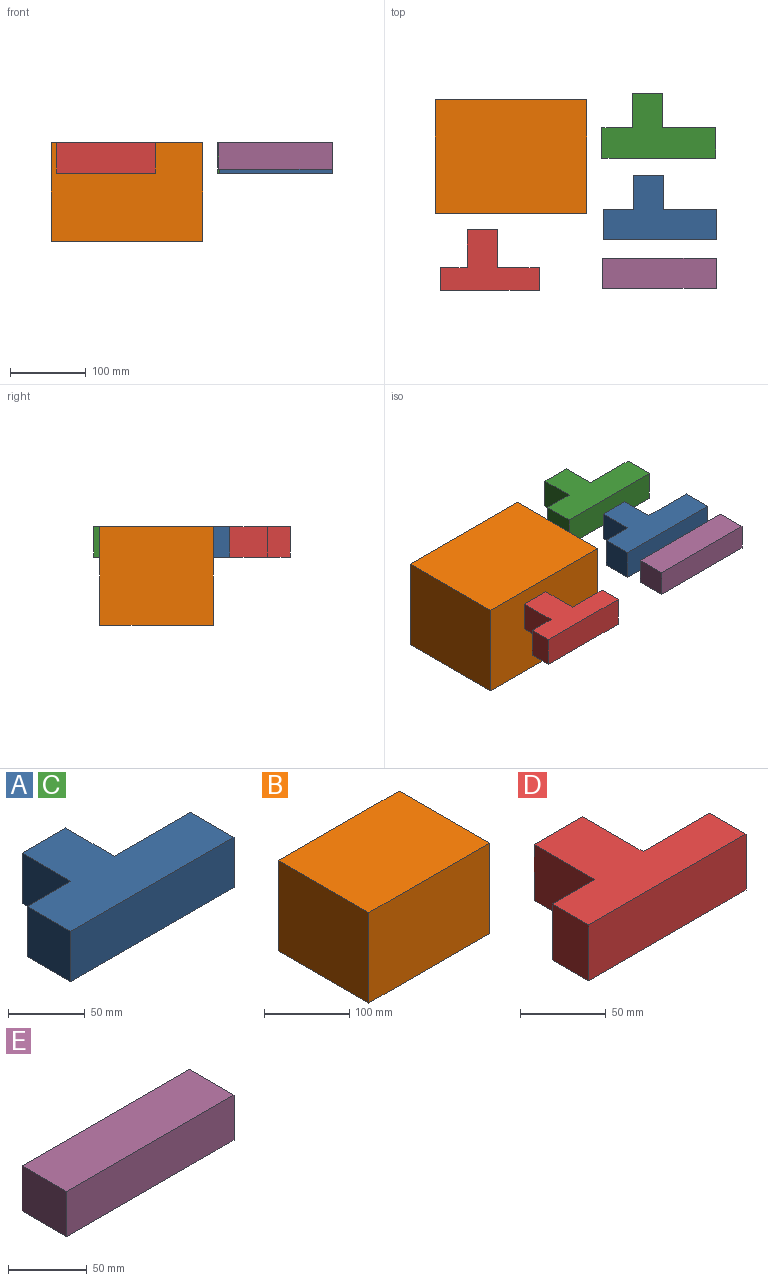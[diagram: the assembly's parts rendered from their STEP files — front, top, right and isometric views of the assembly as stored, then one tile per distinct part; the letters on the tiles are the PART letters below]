
ASSEMBLY  parts=5 mates=4
PART A: 10 faces, bbox 150x85x40 mm
  f0: plane 45x40mm, normal (-1,0,0), area 1800mm2, adj f1,f7,f8,f9
  f1: plane 40x40mm, normal (0,1,0), area 1600mm2, adj f0,f2,f8,f9
  f2: plane 40x40mm, normal (-1,0,0), area 1600mm2, adj f1,f3,f8,f9
  f3: plane 150x40mm, normal (0,-1,0), area 6000mm2, adj f2,f4,f8,f9
  f4: plane 40x40mm, normal (1,0,0), area 1600mm2, adj f3,f5,f8,f9
  f5: plane 70x40mm, normal (0,1,0), area 2800mm2, adj f4,f6,f8,f9
  f6: plane 45x40mm, normal (1,0,0), area 1800mm2, adj f5,f7,f8,f9
  f7: plane 40x40mm, normal (0,1,0), area 1600mm2, adj f0,f6,f8,f9
  f8: plane 150x85mm, normal (0,0,1), area 7800mm2, adj f0,f1,f2,f3,f4,f5,f6,f7
  f9: plane 150x85mm, normal (0,0,-1), area 7800mm2, adj f0,f1,f2,f3,f4,f5,f6,f7
PART B: 6 faces, bbox 200x150x130 mm
  f0: plane 200x130mm, normal (0,1,0), area 26000mm2, adj f1,f3,f4,f5
  f1: plane 150x130mm, normal (-1,0,0), area 19500mm2, adj f0,f2,f4,f5
  f2: plane 200x130mm, normal (0,-1,0), area 26000mm2, adj f1,f3,f4,f5
  f3: plane 150x130mm, normal (1,0,0), area 19500mm2, adj f0,f2,f4,f5
  f4: plane 200x150mm, normal (0,0,1), area 30000mm2, adj f0,f1,f2,f3
  f5: plane 200x150mm, normal (0,0,-1), area 30000mm2, adj f0,f1,f2,f3
PART C: same geometry as A
PART D: 10 faces, bbox 130x80x40 mm
  f0: plane 55x40mm, normal (0,1,0), area 2200mm2, adj f1,f7,f8,f9
  f1: plane 50x40mm, normal (1,0,0), area 2000mm2, adj f0,f2,f8,f9
  f2: plane 40x40mm, normal (0,1,0), area 1600mm2, adj f1,f3,f8,f9
  f3: plane 50x40mm, normal (-1,0,0), area 2000mm2, adj f2,f4,f8,f9
  f4: plane 40x35mm, normal (0,1,0), area 1400mm2, adj f3,f5,f8,f9
  f5: plane 40x30mm, normal (-1,0,0), area 1200mm2, adj f4,f6,f8,f9
  f6: plane 130x40mm, normal (0,-1,0), area 5200mm2, adj f5,f7,f8,f9
  f7: plane 40x30mm, normal (1,0,0), area 1200mm2, adj f0,f6,f8,f9
  f8: plane 130x80mm, normal (0,0,1), area 5900mm2, adj f0,f1,f2,f3,f4,f5,f6,f7
  f9: plane 130x80mm, normal (0,0,-1), area 5900mm2, adj f0,f1,f2,f3,f4,f5,f6,f7
PART E: 6 faces, bbox 150x40x35 mm
  f0: plane 150x35mm, normal (0,1,0), area 5250mm2, adj f1,f3,f4,f5
  f1: plane 40x35mm, normal (-1,0,0), area 1400mm2, adj f0,f2,f4,f5
  f2: plane 150x35mm, normal (0,-1,0), area 5250mm2, adj f1,f3,f4,f5
  f3: plane 40x35mm, normal (1,0,0), area 1400mm2, adj f0,f2,f4,f5
  f4: plane 150x40mm, normal (0,0,1), area 6000mm2, adj f0,f1,f2,f3
  f5: plane 150x40mm, normal (0,0,-1), area 6000mm2, adj f0,f1,f2,f3
PLACE A t=(126.5,4.93,-48.41)mm
PLACE B t=(-69.75,94.42,-138.41)mm
PLACE C t=(125.13,112.49,-48.41)mm
PLACE D t=(-97.73,-81.92,-48.41)mm
PLACE E t=(125.85,-59.44,-43.41)mm
MATE planar C.f8 <-> B.f4  axis (0,0,1) through (121.67,122.3,-8.41)mm
MATE planar C.f8 <-> E.f4  axis (0,0,1) through (121.67,122.3,-8.41)mm
MATE planar D.f8 <-> B.f4  axis (0,0,1) through (-101.12,-53.36,-8.41)mm
MATE planar D.f8 <-> A.f8  axis (0,0,1) through (-101.12,-53.36,-8.41)mm
